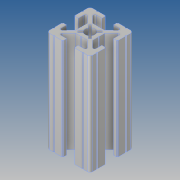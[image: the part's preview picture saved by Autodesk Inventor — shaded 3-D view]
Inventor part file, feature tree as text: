
AUTODESK INVENTOR PART (.ipt)
format: ipt  version: 2018.2 (Build 222227000, 227)  size: 233,472 bytes
history: native  units: mm
features: other x2, extrude x1
ambient origin geometry x8: Origin, YZ Plane, XZ Plane, XY Plane, X Axis, Y Axis, Z Axis, Center Point
bodies: Volumenkörper1 (feature_tree)
feature tree (3):
  other  "90-50-PROFILES-30x30xX.ipt"
  extrude  "Extrusion1"  Depth=10.0mm
  other  "Profil_Skizze"
